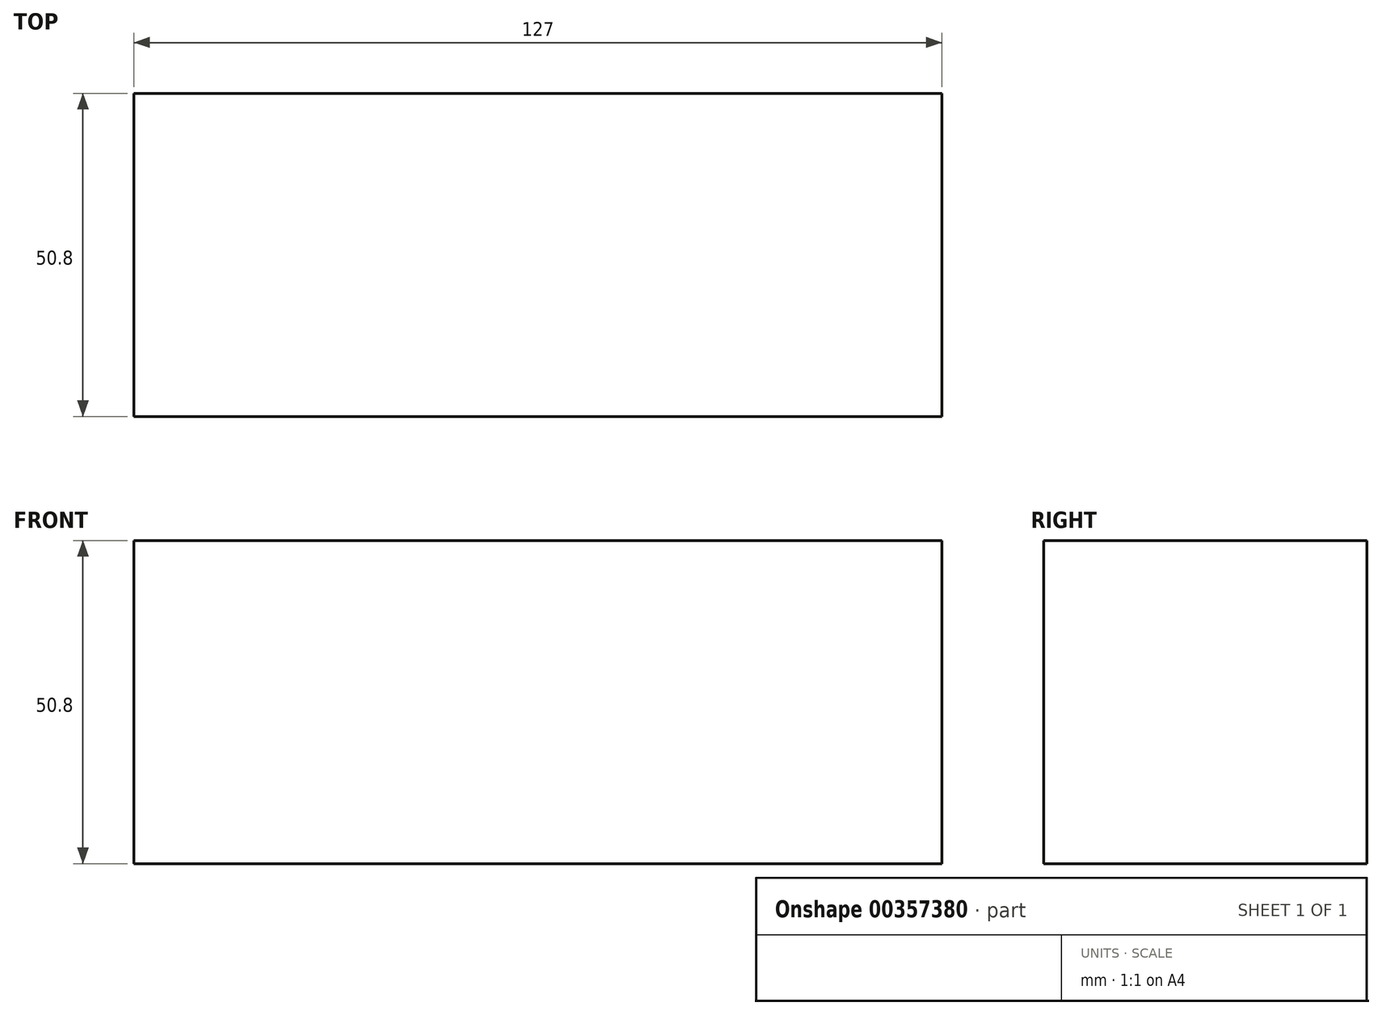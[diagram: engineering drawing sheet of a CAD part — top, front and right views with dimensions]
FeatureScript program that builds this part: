
annotation { "Feature Type Name" : "Feature", "Feature Type Description" : "" }
export const myFeature = defineFeature(function(context is Context, id is Id, definition is map)
    precondition{}
    {
        {
            var Q0;
            Q0=qCreatedBy(makeId("Right.planeOp"),FACE);
            var sketch = newSketch(context, id + "F0", { "sketchPlane" : qUnion([Q0])});
            skLineSegment(sketch, "E0.bottom", {"start": v(0, 0) * mm, "end": v(50.8, 0) * mm});
            skLineSegment(sketch, "E0.top", {"start": v(0, 50.8) * mm, "end": v(50.8, 50.8) * mm});
            skLineSegment(sketch, "E0.left", {"start": v(0, 0) * mm, "end": v(0, 50.8) * mm});
            skLineSegment(sketch, "E0.right", {"start": v(50.8, 0) * mm, "end": v(50.8, 50.8) * mm});
            skSolve(sketch);
        }
        {
            var Q0;
            Q0=makeQuery(id+"F0.imprint","IMPRINT",FACE,{"disambiguationData":[TD([[makeQuery(id+"F0.imprint","IMPRINT",EDGE,{"derivedFrom":sQuery(id+"F0.wireOp",EDGE,"E0.bottom")}),1.0]])]});
            extrude(context, id + "F1", {"entities" : qUnion([Q0]), "depth" : 127 * mm});
        }
    });
